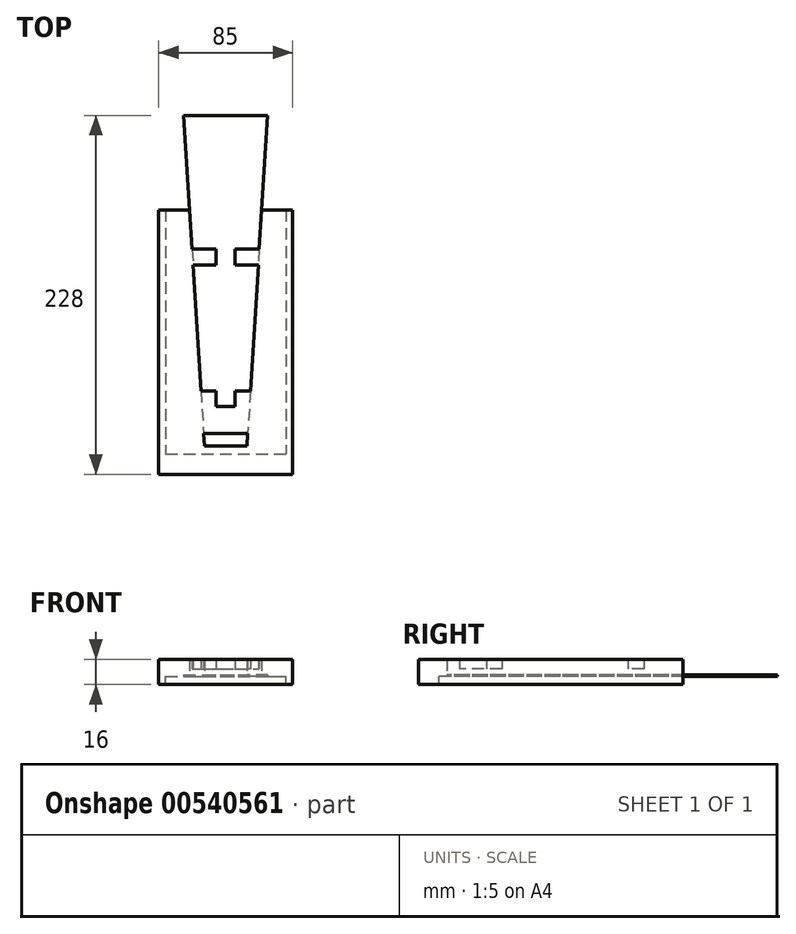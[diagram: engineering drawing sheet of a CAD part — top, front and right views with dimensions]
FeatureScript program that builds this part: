
annotation { "Feature Type Name" : "Feature", "Feature Type Description" : "" }
export const myFeature = defineFeature(function(context is Context, id is Id, definition is map)
    precondition{}
    {
        {
            var Q0;
            Q0=qCreatedBy(makeId("Top.planeOp"),FACE);
            var sketch = newSketch(context, id + "F0", { "sketchPlane" : qUnion([Q0])});
            skLineSegment(sketch, "E0", {"start": v(-26.65, 105) * mm, "end": v(26.65, 105) * mm});
            skLineSegment(sketch, "E1", {"start": v(-13.5, -105) * mm, "end": v(13.5, -105) * mm});
            skLineSegment(sketch, "E2", {"start": v(-26.65, 105) * mm, "end": v(-13.5, -105) * mm});
            skLineSegment(sketch, "E3", {"start": v(26.65, 105) * mm, "end": v(13.5, -105) * mm});
            skLineSegment(sketch, "E4", {"start": v(-22.9, 45) * mm, "end": v(22.9, 45) * mm});
            skLineSegment(sketch, "E5.bottom", {"start": v(-42.5, 45) * mm, "end": v(42.5, 45) * mm});
            skLineSegment(sketch, "E5.top", {"start": v(-38.25, -110) * mm, "end": v(38.25, -110) * mm});
            skLineSegment(sketch, "E5.left", {"start": v(-38.25, 45) * mm, "end": v(-38.25, -110) * mm});
            skLineSegment(sketch, "E5.right", {"start": v(38.25, 45) * mm, "end": v(38.25, -110) * mm});
            skLineSegment(sketch, "E6", {"start": v(-42.5, 45) * mm, "end": v(-42.5, -123) * mm});
            skLineSegment(sketch, "E7", {"start": v(-42.5, -123) * mm, "end": v(42.5, -123) * mm});
            skLineSegment(sketch, "E8", {"start": v(42.5, -123) * mm, "end": v(42.5, 45) * mm});
            skLineSegment(sketch, "E9", {"start": v(-15.07, -80) * mm, "end": v(15.07, -80) * mm});
            skLineSegment(sketch, "E10", {"start": v(-21.33, 20) * mm, "end": v(-6, 20) * mm});
            skLineSegment(sketch, "E11", {"start": v(-20.7, 10) * mm, "end": v(-6, 10) * mm});
            skLineSegment(sketch, "E12", {"start": v(-15.7, -70) * mm, "end": v(-6, -70) * mm});
            skLineSegment(sketch, "E13.right", {"start": v(6, 20) * mm, "end": v(6, 10) * mm});
            skLineSegment(sketch, "E14.trimOffspring", {"start": v(6, 20) * mm, "end": v(21.33, 20) * mm});
            skLineSegment(sketch, "E15.trimOffspring", {"start": v(6, 10) * mm, "end": v(20.7, 10) * mm});
            skLineSegment(sketch, "E16.trimOffspring", {"start": v(6, -70) * mm, "end": v(15.7, -70) * mm});
            skLineSegment(sketch, "E17.trimOffspring", {"start": v(-6, 20) * mm, "end": v(-6, 10) * mm});
            skLineSegment(sketch, "E18.trimOffspring", {"start": v(6, -70) * mm, "end": v(6, -80) * mm});
            skLineSegment(sketch, "E19.trimOffspring", {"start": v(-6, -70) * mm, "end": v(-6, -80) * mm});
            skLineSegment(sketch, "E20", {"start": v(-14, -97) * mm, "end": v(14, -97) * mm});
            skSolve(sketch);
        }
        {
            var Q0;
            Q0=makeQuery(id+"F0.imprint","IMPRINT",FACE,{"disambiguationData":[TD([[makeQuery(id+"F0.imprint","IMPRINT",EDGE,{"derivedFrom":sQuery(id+"F0.wireOp",EDGE,"E5.top")}),-1.0]])]});
            var Q1;
            {var subQ7=sQuery(id+"F0.wireOp",EDGE,"E1");Q1=makeQuery(id+"F0.imprint","IMPRINT",FACE,{"disambiguationData":[TD([[makeQuery(id+"F0.imprint","IMPRINT",EDGE,{"derivedFrom":subQ7}),-1.0]])]});}
            extrude(context, id + "F1", {"entities" : qUnion([Q0, Q1]), "depth" : 11 * mm, "offsetDistance" : 25 * mm});
        }
        {
            var Q0;
            Q0=makeQuery(id+"F0.imprint","IMPRINT",FACE,{"disambiguationData":[TD([[makeQuery(id+"F0.imprint","IMPRINT",EDGE,{"derivedFrom":sQuery(id+"F0.wireOp",EDGE,"E13.right")}),1.0]])]});
            var Q1;
            {var subQ0=sQuery(id+"F0.wireOp",EDGE,"E10");Q1=makeQuery(id+"F0.imprint","IMPRINT",FACE,{"disambiguationData":[TD([[makeQuery(id+"F0.imprint","IMPRINT",EDGE,{"derivedFrom":subQ0}),-1.0]])]});}
            var Q2;
            {var subQ3=sQuery(id+"F0.wireOp",EDGE,"E12");Q2=makeQuery(id+"F0.imprint","IMPRINT",FACE,{"disambiguationData":[TD([[makeQuery(id+"F0.imprint","IMPRINT",EDGE,{"derivedFrom":subQ3}),-1.0]])]});}
            var Q3;
            {var subQ3=sQuery(id+"F0.wireOp",EDGE,"E16.trimOffspring");Q3=makeQuery(id+"F0.imprint","IMPRINT",FACE,{"disambiguationData":[TD([[makeQuery(id+"F0.imprint","IMPRINT",EDGE,{"derivedFrom":subQ3}),-1.0]])]});}
            var Q4;
            {var subQ5=sQuery(id+"F0.wireOp",EDGE,"E20");Q4=makeQuery(id+"F0.imprint","IMPRINT",FACE,{"disambiguationData":[TD([[makeQuery(id+"F0.imprint","IMPRINT",EDGE,{"derivedFrom":subQ5}),1.0]])]});}
            var Q5;
            Q5=makeQuery(id+"F1.opExtrude","CAP_FACE",FACE,{"disambiguationData":[OSD([sQuery(id+"F0.wireOp",EDGE,"E1"),sQuery(id+"F0.wireOp",EDGE,"E2"),sQuery(id+"F0.wireOp",EDGE,"E3"),sQuery(id+"F0.wireOp",EDGE,"E5.bottom"),sQuery(id+"F0.wireOp",EDGE,"E6"),sQuery(id+"F0.wireOp",EDGE,"E7"),sQuery(id+"F0.wireOp",EDGE,"E8")])],"isStart":false});
            extrude(context, id + "F2", {"entities" : qUnion([Q0, Q1, Q2, Q3, Q4]), "operationType" : NewBodyOperationType.ADD, "endBound" : BoundingType.UP_TO_SURFACE, "depth" : 25 * mm, "endBoundEntityFace" : qUnion([Q5]), "offsetDistance" : 25 * mm, "hasSecondDirection" : true, "secondDirectionOppositeDirection" : true, "secondDirectionDepth" : -5 * mm});
        }
        {
            var Q0;
            Q0=makeQuery(id+"F0.imprint","IMPRINT",FACE,{"disambiguationData":[TD([[makeQuery(id+"F0.imprint","IMPRINT",EDGE,{"derivedFrom":sQuery(id+"F0.wireOp",EDGE,"E5.top")}),-1.0]])]});
            extrude(context, id + "F3", {"entities" : qUnion([Q0]), "operationType" : NewBodyOperationType.ADD, "oppositeDirection" : true, "depth" : 5 * mm, "offsetDistance" : 25 * mm});
        }
        {
            var Q0;
            {var subQ5=sQuery(id+"F0.wireOp",EDGE,"E1");Q0=makeQuery(id+"F0.imprint","IMPRINT",FACE,{"disambiguationData":[TD([[makeQuery(id+"F0.imprint","IMPRINT",EDGE,{"derivedFrom":subQ5}),1.0]])]});}
            var Q1;
            {var subQ2=sQuery(id+"F0.wireOp",EDGE,"E10");Q1=makeQuery(id+"F0.imprint","IMPRINT",FACE,{"disambiguationData":[TD([[makeQuery(id+"F0.imprint","IMPRINT",EDGE,{"derivedFrom":subQ2}),1.0]])]});}
            var Q2;
            {var subQ3=sQuery(id+"F0.wireOp",EDGE,"E16.trimOffspring");Q2=makeQuery(id+"F0.imprint","IMPRINT",FACE,{"disambiguationData":[TD([[makeQuery(id+"F0.imprint","IMPRINT",EDGE,{"derivedFrom":subQ3}),-1.0]])]});}
            var Q3;
            {var subQ0=sQuery(id+"F0.wireOp",EDGE,"E0");Q3=makeQuery(id+"F0.imprint","IMPRINT",FACE,{"disambiguationData":[TD([[makeQuery(id+"F0.imprint","IMPRINT",EDGE,{"derivedFrom":subQ0}),-1.0]])]});}
            var Q4;
            Q4=makeQuery(id+"F0.imprint","IMPRINT",FACE,{"disambiguationData":[TD([[makeQuery(id+"F0.imprint","IMPRINT",EDGE,{"derivedFrom":sQuery(id+"F0.wireOp",EDGE,"E13.right")}),1.0]])]});
            var Q5;
            {var subQ0=sQuery(id+"F0.wireOp",EDGE,"E10");Q5=makeQuery(id+"F0.imprint","IMPRINT",FACE,{"disambiguationData":[TD([[makeQuery(id+"F0.imprint","IMPRINT",EDGE,{"derivedFrom":subQ0}),-1.0]])]});}
            var Q6;
            {var subQ3=sQuery(id+"F0.wireOp",EDGE,"E12");Q6=makeQuery(id+"F0.imprint","IMPRINT",FACE,{"disambiguationData":[TD([[makeQuery(id+"F0.imprint","IMPRINT",EDGE,{"derivedFrom":subQ3}),-1.0]])]});}
            var Q7;
            {var subQ5=sQuery(id+"F0.wireOp",EDGE,"E20");Q7=makeQuery(id+"F0.imprint","IMPRINT",FACE,{"disambiguationData":[TD([[makeQuery(id+"F0.imprint","IMPRINT",EDGE,{"derivedFrom":subQ5}),1.0]])]});}
            extrude(context, id + "F4", {"entities" : qUnion([Q0, Q1, Q2, Q3, Q4, Q5, Q6, Q7]), "depth" : 1 * mm, "offsetDistance" : 25 * mm});
        }
    });
